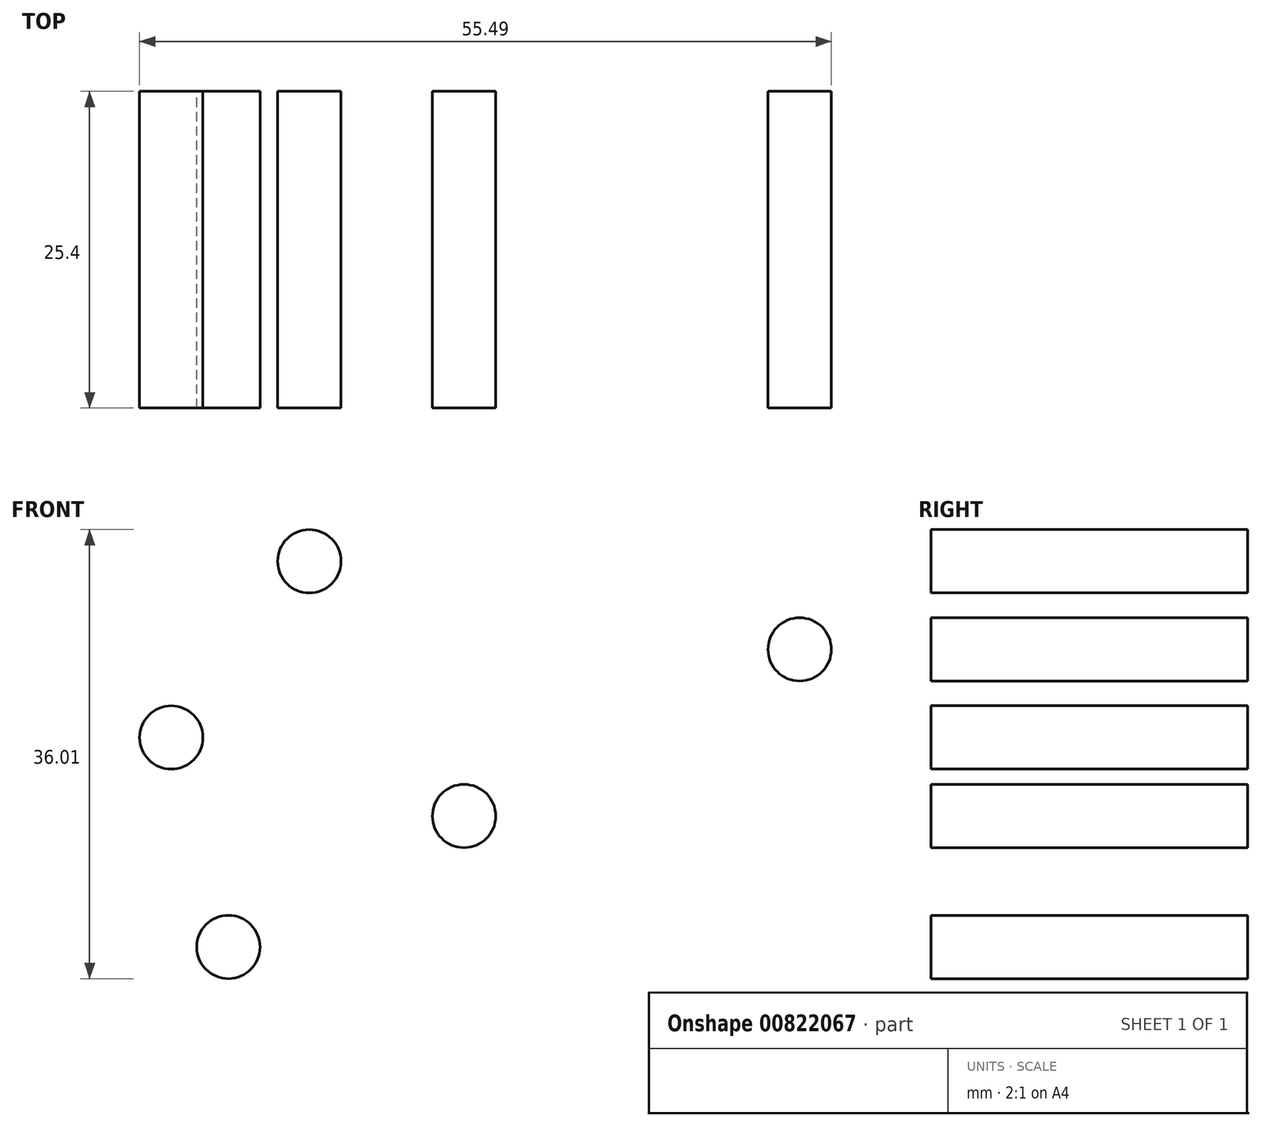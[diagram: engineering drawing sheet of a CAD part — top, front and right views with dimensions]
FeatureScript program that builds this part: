
annotation { "Feature Type Name" : "Feature", "Feature Type Description" : "" }
export const myFeature = defineFeature(function(context is Context, id is Id, definition is map)
    precondition{}
    {
        {
            var Q0;
            Q0=qCreatedBy(makeId("Front.planeOp"),FACE);
            var sketch = newSketch(context, id + "F0", { "sketchPlane" : qUnion([Q0])});
            skCircle(sketch, "E0", {"center": v(-33.7, 23.01) * mm, "radius": 2.54 * mm});
            skCircle(sketch, "E1", {"center": v(-6.78, 36.38) * mm, "radius": 2.54 * mm});
            skCircle(sketch, "E2", {"center": v(-46.12, 43.44) * mm, "radius": 2.54 * mm});
            skCircle(sketch, "E3", {"center": v(-57.2, 29.31) * mm, "radius": 2.54 * mm});
            skCircle(sketch, "E4", {"center": v(-52.6, 12.5) * mm, "radius": 2.54 * mm});
            skSolve(sketch);
        }
        {
            var Q0;
            Q0=qSketchRegion(id+"F0",true);
            extrude(context, id + "F1", {"entities" : qUnion([Q0]), "depth" : 25.4 * mm, "offsetDistance" : 25.4 * mm});
        }
    });
